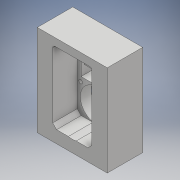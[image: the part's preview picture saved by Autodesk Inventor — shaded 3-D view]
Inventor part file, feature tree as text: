
AUTODESK INVENTOR PART (.ipt)
format: ipt  version: 2018 (Build 220112000, 112)  size: 423,424 bytes
history: native  units: mm
features: sketch x21, extrude x18, projected_geometry x18, hole x3, fillet x3, chamfer x1, mirror x1
ambient origin geometry x8: Origin, YZ Plane, XZ Plane, XY Plane, X Axis, Y Axis, Z Axis, Center Point
bodies: Solid1 (feature_tree)
feature tree (65):
  extrude  "Extrusion1"  Depth=45.0mm
  extrude  "Extrusion2"  Depth=1.95mm
  hole  "Hole1"  [1 undecoded]
  hole  "Hole2"  [1 undecoded]
  fillet  "Fillet1"  Radius=14.0mm
  extrude  "Extrusion3"  Depth=18.5mm
  extrude  "Extrusion4"  Depth=10.0mm
  extrude  "Extrusion5"  Depth=2.195mm
  extrude  "Extrusion6"  Depth=20.5mm
  hole  "Hole3"  [1 undecoded]
  extrude  "Extrusion7"  Depth=0.5mm
  extrude  "Extrusion8"  Depth=5.0mm TaperAngle=0.0deg
  extrude  "Extrusion9"  Depth=10.0mm
  extrude  "Extrusion10"  Depth=10.0mm
  extrude  "Extrusion11"  Depth=14.5mm
  extrude  "Extrusion12"  Depth=20.0mm
  extrude  "Extrusion13"  Depth=5.0mm
  extrude  "Extrusion14"  Depth=5.0mm
  extrude  "Extrusion15"  Depth=5.0mm
  extrude  "Extrusion16"  Depth=22.55mm
  extrude  "Extrusion17"  Depth=22.55mm
  chamfer  "Chamfer1"  Distance=4.0mm
  fillet  "Fillet7"  Radius=1.0mm
  fillet  "Fillet8"  Radius=20.7mm
  mirror  "Mirror1"
  extrude  "Extrusion18"  Depth=22.55mm
  sketch  "Sketch1"  dims[d0=24.5mm d1=45.0mm]
  sketch  "Sketch2"  dims[d2=1.95mm d3=0.0mm d4=2.25mm]
  projected_geometry  "Projected Loop1"
  sketch  "Sketch3"  dims[d5=20.0mm d6=2.25mm]
  projected_geometry  "Projected Loop2"
  sketch  "Sketch4"  dims[d7=5.25mm d8=5.25mm d9=14.0mm]
  projected_geometry  "Projected Loop3"
  sketch  "Sketch5"  dims[d10=5.25mm d11=18.5mm]
  projected_geometry  "Projected Loop4"
  sketch  "Sketch6"  dims[d12=10.0mm d13=0.0mm d14=20.5mm]
  projected_geometry  "Projected Loop5"
  sketch  "Sketch7"  dims[d15=2.0mm d16=2.195mm]
  projected_geometry  "Projected Loop6"
  sketch  "Sketch8"  dims[d17=2.0mm]
  projected_geometry  "Projected Loop7"
  sketch  "Sketch9"  dims[d18=2.4mm d19=6.0mm d20=4.4mm d21=2.0mm d22=90.0deg d23=8.0mm d24=20.594885mm d25=20.5mm]
  projected_geometry  "Projected Loop8"
  projected_geometry  "Projected Loop9"
  sketch  "Sketch10"  dims[d26=26.65mm d27=2.0mm]
  projected_geometry  "Projected Loop10"
  projected_geometry  "Projected Loop11"
  sketch  "Sketch11"  dims[d28=2.0mm]
  projected_geometry  "Projected Loop12"
  sketch  "Sketch12"  dims[d29=2.4mm d30=6.0mm d31=4.4mm d32=2.0mm d33=90.0deg d34=8.0mm d35=20.594885mm d36=0.5mm]
  sketch  "Sketch13"  dims[d37=18.0mm d38=5.0mm d39=0.0mm]
  sketch  "Sketch14"  dims[d41=10.0mm d42=0.0mm d43=24.5mm]
  projected_geometry  "Projected Loop13"
  sketch  "Sketch15"  dims[d44=1.15mm d45=0.0mm d46=10.0mm]
  sketch  "Sketch16"  dims[d47=21.0mm d48=14.5mm]
  projected_geometry  "Projected Loop14"
  sketch  "Sketch17"  dims[d49=20.0mm d50=14.5mm]
  projected_geometry  "Projected Loop15"
  sketch  "Sketch18"  dims[d51=24.5mm d52=5.0mm]
  projected_geometry  "Projected Loop16"
  sketch  "Sketch19"  dims[d53=5.0mm d54=2.25mm]
  projected_geometry  "Projected Loop17"
  sketch  "Sketch20"  dims[d55=2.25mm d56=5.0mm]
  projected_geometry  "Projected Loop18"
  sketch  "Sketch22"  dims[d57=5.0mm d58=9.0mm d59=14.75mm d60=4.0mm d61=1.0mm d62=0.0mm d63=20.7mm d64=2.4mm d65=6.0mm d66=4.4mm d67=2.0mm d68=90.0deg d69=8.0mm d70=20.594885mm d72=32.0mm d73=5.0mm d74=0.0mm d75=1.0mm d76=0.0mm d77=12.25mm d78=0.0mm d80=8.0mm d81=4.5mm d82=0.0mm d84=0.2mm d85=0.0mm d86=21.0mm d87=0.5mm d88=0.0mm d91=8.0mm d92=0.0mm d93=5.0mm d94=0.0mm d95=5.0mm d96=0.0mm d98=0.2mm d99=0.0mm d100=0.2mm d101=0.0mm d102=2.5mm d103=2.0mm d104=45.0deg d105=1.5mm d114=0.5mm d115=22.55mm d116=0.0mm]
note: 3 required parameter values undecoded (feature->parameter linkage not recoverable at this tier; creation-order binding heuristic only, values carry confidence <= 0.55)
